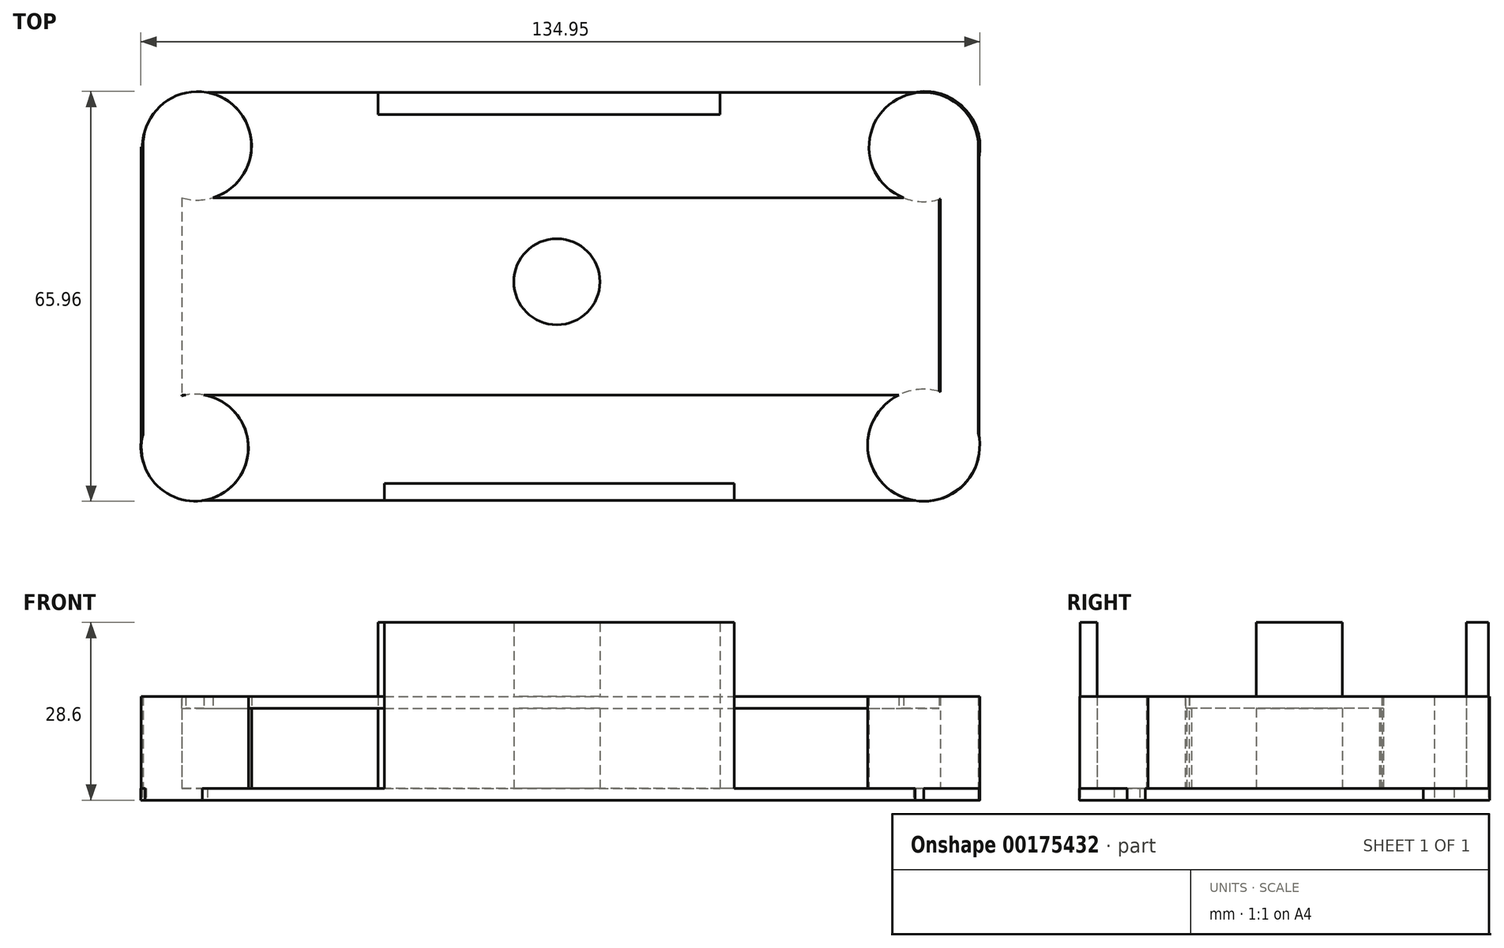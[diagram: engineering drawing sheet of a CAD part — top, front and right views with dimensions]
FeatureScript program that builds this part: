
annotation { "Feature Type Name" : "Feature", "Feature Type Description" : "" }
export const myFeature = defineFeature(function(context is Context, id is Id, definition is map)
    precondition{}
    {
        {
            var Q0;
            Q0=qCreatedBy(makeId("Top.planeOp"),FACE);
            var sketch = newSketch(context, id + "F0", { "sketchPlane" : qUnion([Q0])});
            skLineSegment(sketch, "E0.bottom", {"start": v(60.9, 30.45) * mm, "end": v(-58.12, 30.45) * mm});
            skLineSegment(sketch, "E0.top", {"start": v(60.52, -35.22) * mm, "end": v(-58.97, -35.22) * mm});
            skLineSegment(sketch, "E0.left", {"start": v(67.87, 23.48) * mm, "end": v(67.87, -27.86) * mm});
            skLineSegment(sketch, "E0.right", {"start": v(-66.86, 21.72) * mm, "end": v(-66.86, -27.33) * mm});
            skLineSegment(sketch, "E1.bottom", {"start": v(4.74, 30.45) * mm, "end": v(3.89, 30.45) * mm});
            skLineSegment(sketch, "E1.top", {"start": v(4.74, 23.69) * mm, "end": v(3.89, 23.69) * mm});
            skLineSegment(sketch, "E2.top", {"start": v(-66.86, 21.72) * mm, "end": v(-66.64, 21.72) * mm});
            skLineSegment(sketch, "E2.right", {"start": v(-58.12, 30.45) * mm, "end": v(-58.12, 30.24) * mm});
            skLineSegment(sketch, "E3.bottom", {"start": v(-58.97, -35.22) * mm, "end": v(-58.12, -35.22) * mm});
            skLineSegment(sketch, "E3.left", {"start": v(-66.86, -27.33) * mm, "end": v(-66.86, -26.48) * mm});
            skLineSegment(sketch, "E4.bottom", {"start": v(60.9, 30.45) * mm, "end": v(59.13, 30.45) * mm});
            skLineSegment(sketch, "E4.left", {"start": v(67.87, 23.48) * mm, "end": v(67.87, 21.72) * mm});
            skLineSegment(sketch, "E5.bottom", {"start": v(60.52, -35.22) * mm, "end": v(59.13, -35.22) * mm});
            skLineSegment(sketch, "E5.left", {"start": v(67.87, -27.86) * mm, "end": v(67.87, -26.48) * mm});
            skArc(sketch, "E6", {"start": v(-58.12, 30.24) * mm, "mid": v(-64.15, 27.74) * mm, "end": v(-66.64, 21.72) * mm});
            skArc(sketch, "E7", {"start": v(-66.86, -25.64) * mm, "mid": v(-64.33, -32.7) * mm, "end": v(-57.27, -35.22) * mm});
            skArc(sketch, "E8", {"start": v(67.87, 19.96) * mm, "mid": v(65.44, 28.02) * mm, "end": v(57.37, 30.45) * mm});
            skArc(sketch, "E9", {"start": v(57.75, -35.22) * mm, "mid": v(65.39, -32.74) * mm, "end": v(67.87, -25.1) * mm});
            skSolve(sketch);
        }
        {
            var Q0;
            Q0 = qSketchRegion(id + "F0", true);
            extrude(context, id + "F1", {"entities" : qUnion([Q0]), "depth" : 1.9 * mm});
        }
        {
            var Q0;
            Q0=qCreatedBy(makeId("Top.planeOp"),FACE);
            var sketch = newSketch(context, id + "F2", { "sketchPlane" : qUnion([Q0])});
            skCircle(sketch, "E10", {"center": v(-57.83, 21.88) * mm, "radius": 8.73 * mm});
            skCircle(sketch, "E11", {"center": v(-58.22, -26.7) * mm, "radius": 8.6 * mm});
            skCircle(sketch, "E12", {"center": v(59, -26.31) * mm, "radius": 9.01 * mm});
            skCircle(sketch, "E13", {"center": v(59, 21.69) * mm, "radius": 8.8 * mm});
            skLineSegment(sketch, "E14.bottom", {"start": v(-66.56, 21.7) * mm, "end": v(-60.34, 21.7) * mm});
            skLineSegment(sketch, "E14.top", {"start": v(-66.56, -26.7) * mm, "end": v(-60.34, -26.7) * mm});
            skLineSegment(sketch, "E14.left", {"start": v(-66.56, 21.7) * mm, "end": v(-66.56, -26.7) * mm});
            skLineSegment(sketch, "E14.right", {"start": v(-60.34, 21.7) * mm, "end": v(-60.34, -26.7) * mm});
            skLineSegment(sketch, "E15.bottom", {"start": v(67.78, 21.68) * mm, "end": v(61.69, 21.68) * mm});
            skLineSegment(sketch, "E15.top", {"start": v(67.78, -26.31) * mm, "end": v(61.69, -26.31) * mm});
            skLineSegment(sketch, "E15.left", {"start": v(67.78, 21.68) * mm, "end": v(67.78, -26.31) * mm});
            skLineSegment(sketch, "E15.right", {"start": v(61.69, 21.68) * mm, "end": v(61.69, -26.31) * mm});
            skSolve(sketch);
        }
        {
            var Q0;
            Q0 = qSketchRegion(id + "F2", true);
            extrude(context, id + "F3", {"entities" : qUnion([Q0]), "operationType" : NewBodyOperationType.ADD, "depth" : 16.7 * mm});
        }
        {
            var Q0;
            {var subQ0=sQuery(id+"F0.wireOp",EDGE,"E0.left");var subQ1=sQuery(id+"F0.wireOp",EDGE,"E1.bottom");var subQ2=sQuery(id+"F0.wireOp",EDGE,"E0.bottom");var subQ3=sQuery(id+"F0.wireOp",EDGE,"E0.top");var subQ4=sQuery(id+"F0.wireOp",EDGE,"E8");Q0=makeQuery(id+"F3.boolean.opBoolean","SPLIT",FACE,{"disambiguationData":[TD([makeQuery(id+"F1.opExtrude","SWEPT_FACE",FACE,{"disambiguationData":[OSD([subQ3])]})])],"derivedFrom":makeQuery(id+"F1.opExtrude","CAP_FACE",FACE,{"disambiguationData":[OSD([subQ2,subQ3,subQ0,sQuery(id+"F0.wireOp",EDGE,"E0.right"),subQ1,sQuery(id+"F0.wireOp",EDGE,"E2.top"),sQuery(id+"F0.wireOp",EDGE,"E2.right"),sQuery(id+"F0.wireOp",EDGE,"E6"),sQuery(id+"F0.wireOp",EDGE,"E7"),subQ4,sQuery(id+"F0.wireOp",EDGE,"E9")])],"isStart":false})});}
            var sketch = newSketch(context, id + "F4", { "sketchPlane" : qUnion([Q0])});
            skCircle(sketch, "E16", {"center": v(0, 0) * mm, "radius": 6.92 * mm});
            skLineSegment(sketch, "E17.bottom", {"start": v(0, -35.22) * mm, "end": v(-27.76, -35.22) * mm});
            skLineSegment(sketch, "E17.top", {"start": v(0, -32.48) * mm, "end": v(-27.76, -32.48) * mm});
            skLineSegment(sketch, "E17.left", {"start": v(0, -35.22) * mm, "end": v(0, -32.48) * mm});
            skLineSegment(sketch, "E17.right", {"start": v(-27.76, -35.22) * mm, "end": v(-27.76, -32.48) * mm});
            skLineSegment(sketch, "E18.bottom", {"start": v(0, -35.22) * mm, "end": v(28.53, -35.22) * mm});
            skLineSegment(sketch, "E18.top", {"start": v(0, -32.48) * mm, "end": v(28.53, -32.48) * mm});
            skLineSegment(sketch, "E18.right", {"start": v(28.53, -35.22) * mm, "end": v(28.53, -32.48) * mm});
            skLineSegment(sketch, "E19.bottom", {"start": v(0, 30.45) * mm, "end": v(26.22, 30.45) * mm});
            skLineSegment(sketch, "E19.top", {"start": v(0, 26.9) * mm, "end": v(26.22, 26.9) * mm});
            skLineSegment(sketch, "E19.left", {"start": v(0, 30.45) * mm, "end": v(0, 26.9) * mm});
            skLineSegment(sketch, "E19.right", {"start": v(26.22, 30.45) * mm, "end": v(26.22, 26.9) * mm});
            skLineSegment(sketch, "E20.bottom", {"start": v(0, 30.45) * mm, "end": v(-28.72, 30.45) * mm});
            skLineSegment(sketch, "E20.top", {"start": v(0, 26.9) * mm, "end": v(-28.72, 26.9) * mm});
            skLineSegment(sketch, "E20.right", {"start": v(-28.72, 30.45) * mm, "end": v(-28.72, 26.9) * mm});
            skSolve(sketch);
        }
        {
            var Q0;
            Q0 = qSketchRegion(id + "F4", true);
            extrude(context, id + "F5", {"entities" : qUnion([Q0]), "operationType" : NewBodyOperationType.ADD, "depth" : 26.7 * mm});
        }
        {
            var Q0;
            Q0=makeQuery(id+"F3.opExtrude","CAP_FACE",FACE,{"disambiguationData":[OSD([sQuery(id+"F2.wireOp",EDGE,"E10"),sQuery(id+"F2.wireOp",EDGE,"E11"),sQuery(id+"F2.wireOp",EDGE,"E14.left"),sQuery(id+"F2.wireOp",EDGE,"E14.right")])],"isStart":false});
            var sketch = newSketch(context, id + "F6", { "sketchPlane" : qUnion([Q0])});
            skPoint(sketch, "E21.firstSnap0", {"position": v(-50.88, 27.16) * mm});
            skLineSegment(sketch, "E22.bottom", {"start": v(-60.34, 13.52) * mm, "end": v(61.5, 13.52) * mm});
            skLineSegment(sketch, "E22.top", {"start": v(-60.34, -18.22) * mm, "end": v(61.5, -18.22) * mm});
            skLineSegment(sketch, "E22.left", {"start": v(-60.34, 13.52) * mm, "end": v(-60.34, -18.22) * mm});
            skLineSegment(sketch, "E22.right", {"start": v(61.5, 13.52) * mm, "end": v(61.5, -18.22) * mm});
            skSolve(sketch);
        }
        {
            var Q0;
            Q0 = qSketchRegion(id + "F6", true);
            extrude(context, id + "F7", {"entities" : qUnion([Q0]), "operationType" : NewBodyOperationType.ADD, "oppositeDirection" : true, "depth" : 1.9 * mm});
        }
    });
